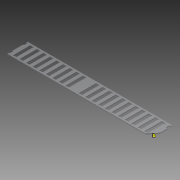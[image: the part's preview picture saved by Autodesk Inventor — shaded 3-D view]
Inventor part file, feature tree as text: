
AUTODESK INVENTOR PART (.ipt)
format: ipt  version: 2013 (Build 170138000, 138)  size: 244,224 bytes
history: native  units: in
note: dims shown in document units (in); Inventor stores cm internally (conversion verified against a paired STEP export)
features: extrude x5, sketch x5, projected_geometry x2
ambient origin geometry x8: Origin, YZ Plane, XZ Plane, XY Plane, X Axis, Y Axis, Z Axis, Center Point
bodies: Solid1 (feature_tree)
feature tree (12):
  extrude  "Extrusion1"  Depth=22.0in
  extrude  "Extrusion2"  Depth=0.5in
  extrude  "Extrusion3"  Depth=0.5in
  extrude  "Extrusion4"  Depth=0.125in TaperAngle=0.0deg
  extrude  "Extrusion5"  Depth=0.5in
  sketch  "Sketch1"  dims[d0=3.125in d1=22.0in]
  sketch  "Sketch3"  dims[d2=0.125in d3=0.0in d4=0.5in]
  sketch  "Sketch4"  dims[d5=0.25in d6=0.5in]
  projected_geometry  "Projected Loop1"
  projected_geometry  "Projected Loop2"
  sketch  "Sketch5"  dims[d7=0.25in d8=0.125in d9=0.0in]
  sketch  "Sketch6"  dims[d10=0.25in d11=0.0in d12=0.5in d14=0.625in d15=0.25in d16=0.25in d17=8.2677in d19=1.0in d20=0.3937in d22=1.0in d24=1.0in d25=0.0in d26=0.3436in d27=1.0in d28=1.0in d29=0.0in]
